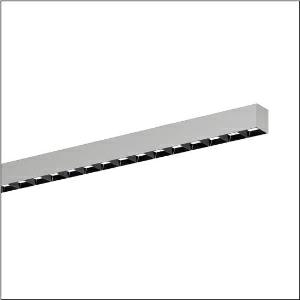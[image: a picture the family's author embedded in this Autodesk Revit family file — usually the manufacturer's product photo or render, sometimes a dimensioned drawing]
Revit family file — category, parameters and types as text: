
# Revit family: silica_21_51mx21tctas
name_source: partatom
category: Lighting Fixtures
units: mm (PartAtom-declared; Revit-internal decimal feet)

## family parameters
Cut with Voids When Loaded = No
Host = Face
Light Source = No
Part Type = Normal
Room Calculation Point = No
Round Connector Dimension = Use Diameter
Shared = No

## types (1)
- --- (1 x LED, 9300 lm, 80.5 W, 6500K)
    Apparent Load = 81 VA
    CIE Flux Codes = 85 99 100 100 100
    Color Rendering = 80
    Color Temperature = 6500K
    Default Elevation = 1800 mm
    Description = Silica 21, office luminaire, primary light control with darklight reflector, of PMMA, black, CAT 2 (L<= 3000cd/m²), light emission: direct distribution, primary light characteristic: symmetric, installation type: surface-mounted, LED, rated luminous flux: 9.300lm, luminous efficacy: 110lm/W, light colour: 8tw, colour temperature: 2700..6500K, control gear: DALI DT8, with terminal, 3+2-pole, max. 2.5mm², mains connection: 220..240V, AC, 50/60Hz, rated input power: 84.6W, luminaire housing, of aluminium, metallic grey (RAL 9006), length: 3.004mm, width: 53mm, height: 53mm, protection rating (complete): IP20, insulation class (complete): insulation class I (protective earthing), certification: CE, permissible operating ambient temperature: 0..+35°C, standard: EN 50419, packaging unit: 1 piece
    Height = 53 mm
    Lamp = 1 x LED
    Lamp Light Flux = 9300 lm
    Lamp Power = 80.5 W
    Lamp count = 1
    Length = 3004 mm
    Luminous efficacy = 116 lm/W
    Manufacturer = Siteco
    ModVariant = No
    Model = 51MX21TCTAS
    Mounting Place = Ceiling
    Mounting Type = Surface mounted
    Number of Poles = 1
    OnlyDefault = Yes
    Power Factor = 1
    Product Name = Silica 21
    Product group = office luminaire | ceiling mounted
    ProductGroupID = 301
    Protection Class = Protection class I
    Protection Degree = IP 20
    RLX_Detail_Level = 1
    RLX_Emergency_Light_Flux = 0 lm
    RLX_Emergency_Type = 0
    RLX_Emergency_Type_DB = No
    RlxData = <blob elided: 61193 chars, md5=03e78e98>
    Socket = socket
    Standby Power = 0 W
    System Light Flux = 9300 lm
    System Power = 81 W
    Type Comments = individual setting
    Type Image = l_1335929.jpg
    URL = http://relux.com
    VarID = @adj_141091
    Voltage = 0 V
    Weight = 0.00 kg
    Width = 53 mm

## geometry (parser evidence)
native form markers: Blend x4, Sweep x10
no freeform markers — native parametric forms only
